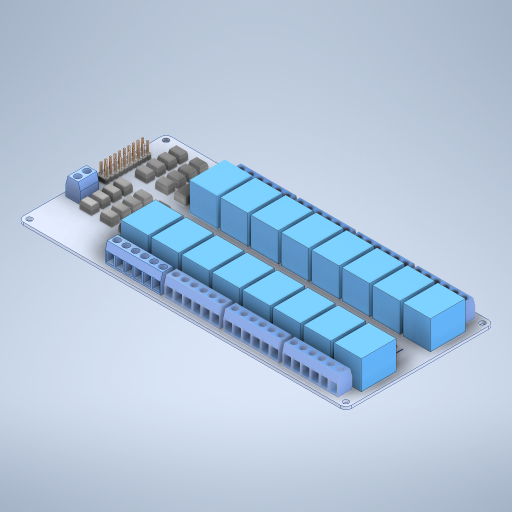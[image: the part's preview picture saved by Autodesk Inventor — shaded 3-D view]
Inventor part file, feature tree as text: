
AUTODESK INVENTOR PART (.ipt)
format: ipt  version: 2024 (Build 280153000, 153)  size: 1,530,368 bytes
history: native  units: in
note: dims shown in document units (in); Inventor stores cm internally (conversion verified against a paired STEP export)
features: other x48, mirror x12, chamfer x4
ambient origin geometry x8: Origin, YZ Plane, XZ Plane, XY Plane, X Axis, Y Axis, Z Axis, Center Point
bodies: Solid1 (feature_tree), Solid2 (feature_tree), Solid3 (feature_tree), Solid4 (feature_tree), Solid5 (feature_tree), Solid6 (feature_tree), Solid7 (feature_tree), Solid8 (feature_tree), Solid9 (feature_tree), Solid10 (feature_tree), Solid11 (feature_tree), Solid12 (feature_tree), Solid13 (feature_tree), Solid14 (feature_tree), Solid15 (feature_tree), Solid16 (feature_tree), Solid17 (feature_tree), Solid18 (feature_tree), Solid19 (feature_tree), Solid20 (feature_tree), Solid21 (feature_tree), Solid22 (feature_tree), Solid23 (feature_tree), Solid24 (feature_tree), Solid25 (feature_tree), Solid26 (feature_tree), Solid27 (feature_tree), Solid28 (feature_tree), Solid29 (feature_tree), Solid30 (feature_tree), Solid31 (feature_tree), Solid32 (feature_tree), Solid33 (feature_tree), Solid34 (feature_tree), Solid35 (feature_tree), Solid36 (feature_tree), Solid37 (feature_tree), Solid38 (feature_tree), Solid39 (feature_tree), Solid40 (feature_tree), Solid41 (feature_tree), Solid42 (feature_tree), Solid43 (feature_tree), Solid44 (feature_tree), Solid45 (feature_tree), Solid46 (feature_tree), Solid47 (feature_tree), Solid48 (feature_tree), Solid49 (feature_tree), Solid50 (feature_tree), Solid51 (feature_tree), Solid52 (feature_tree), Solid53 (feature_tree), Solid54 (feature_tree), Solid55 (feature_tree), Solid56 (feature_tree), Solid57 (feature_tree), Solid58 (feature_tree), Solid59 (feature_tree), Solid60 (feature_tree), Solid61 (feature_tree), Solid62 (feature_tree), Solid63 (feature_tree), Solid64 (feature_tree)
feature tree (64):
  other  "Boss-Extrude4"
  chamfer  "Chamfer2"  [1 undecoded]
  other  "LPattern1[1]"
  other  "LPattern1[2]"
  other  "LPattern1[3]"
  other  "LPattern1[4]"
  other  "LPattern1[5]"
  other  "LPattern1[6]"
  other  "LPattern1[7]"
  other  "LPattern1[8]"
  other  "LPattern1[9]"
  other  "LPattern1[10]"
  other  "LPattern1[11]"
  other  "LPattern1[12]"
  other  "LPattern1[13]"
  other  "LPattern1[14]"
  other  "LPattern1[15]"
  other  "LPattern1[16]"
  other  "LPattern1[17]"
  other  "LPattern1[18]"
  chamfer  "Chamfer3"  [1 undecoded]
  other  "LPattern2[1]"
  other  "LPattern2[2]"
  other  "LPattern2[3]"
  other  "LPattern3[1]"
  other  "LPattern3[2]"
  other  "LPattern3[3]"
  other  "LPattern3[4]"
  other  "LPattern3[5]"
  other  "LPattern3[6]"
  other  "LPattern3[7]"
  other  "LPattern3[8]"
  other  "LPattern3[9]"
  other  "LPattern3[10]"
  other  "LPattern3[11]"
  other  "LPattern3[12]"
  chamfer  "Chamfer4"  [1 undecoded]
  chamfer  "Chamfer5"  [1 undecoded]
  other  "Boss-Extrude8"
  other  "LPattern4[1]"
  other  "LPattern4[2]"
  other  "LPattern4[3]"
  other  "LPattern4[4]"
  other  "LPattern4[5]"
  other  "LPattern4[6]"
  other  "LPattern4[7]"
  mirror  "Mirror1[1]"
  mirror  "Mirror1[2]"
  mirror  "Mirror1[3]"
  mirror  "Mirror1[4]"
  mirror  "Mirror1[5]"
  mirror  "Mirror1[6]"
  mirror  "Mirror1[7]"
  mirror  "Mirror1[8]"
  other  "Cut-Extrude3"
  other  "LPattern5"
  other  "LPattern6[1]"
  other  "LPattern6[2]"
  other  "LPattern6[3]"
  mirror  "Mirror2[1]"
  mirror  "Mirror2[2]"
  mirror  "Mirror2[3]"
  mirror  "Mirror2[4]"
  other  "Cut-Extrude6"
note: 4 required parameter values undecoded (feature->parameter linkage not recoverable at this tier; creation-order binding heuristic only, values carry confidence <= 0.55)
